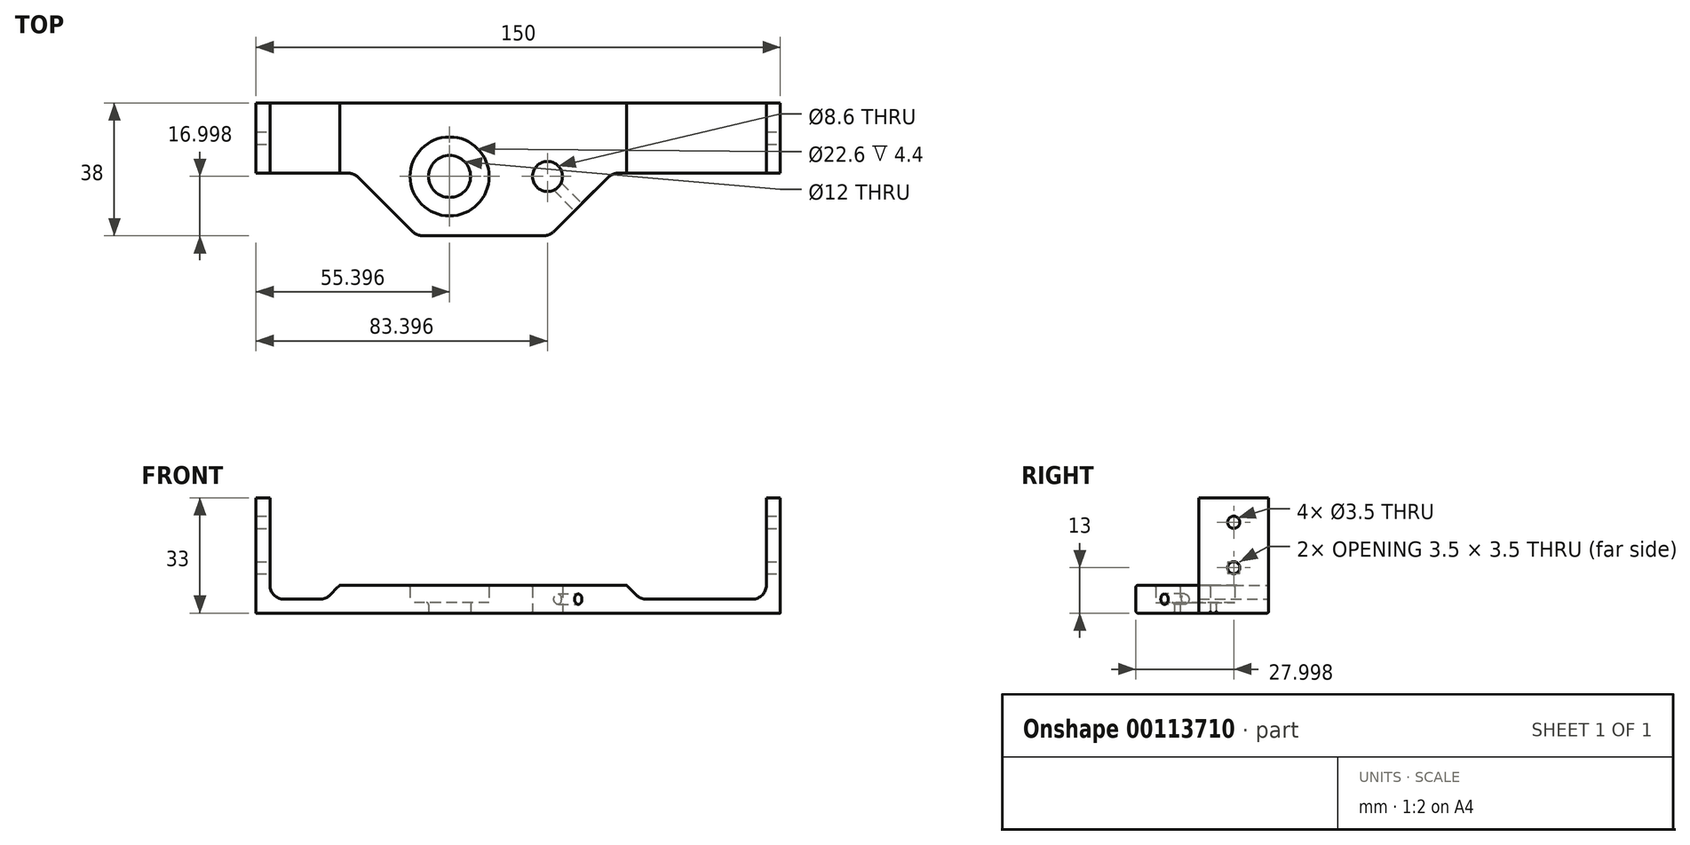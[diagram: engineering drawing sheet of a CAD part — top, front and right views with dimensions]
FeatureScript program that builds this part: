
annotation { "Feature Type Name" : "Feature", "Feature Type Description" : "" }
export const myFeature = defineFeature(function(context is Context, id is Id, definition is map)
    precondition{}
    {
        {
            var Q0;
            Q0=qCreatedBy(makeId("Top.planeOp"),FACE);
            var sketch = newSketch(context, id + "F0", { "sketchPlane" : qUnion([Q0])});
            skLineSegment(sketch, "E0.bottom", {"start": v(-77.83, 12.2) * mm, "end": v(72.17, 12.2) * mm});
            skLineSegment(sketch, "E0.left", {"start": v(-77.83, 12.2) * mm, "end": v(-77.83, -7.8) * mm});
            skLineSegment(sketch, "E0.right", {"start": v(72.17, 12.2) * mm, "end": v(72.17, -7.8) * mm});
            skCircle(sketch, "E1", {"center": v(-22.43, -8.8) * mm, "radius": 6 * mm});
            skCircle(sketch, "E2", {"center": v(5.57, -8.8) * mm, "radius": 4.3 * mm});
            skCircle(sketch, "E3", {"center": v(-22.43, -8.8) * mm, "radius": 11.3 * mm});
            skLineSegment(sketch, "E4", {"start": v(-77.83, -7.8) * mm, "end": v(-49.83, -7.8) * mm});
            skLineSegment(sketch, "E5", {"start": v(-49.83, -7.8) * mm, "end": v(-31.83, -25.8) * mm});
            skLineSegment(sketch, "E6", {"start": v(-31.83, -25.8) * mm, "end": v(6.17, -25.8) * mm});
            skLineSegment(sketch, "E7", {"start": v(6.17, -25.8) * mm, "end": v(24.17, -7.8) * mm});
            skLineSegment(sketch, "E8", {"start": v(24.17, -7.8) * mm, "end": v(72.17, -7.8) * mm});
            skSolve(sketch);
        }
        {
            var Q0;
            Q0=makeQuery(id+"F0.imprint","IMPRINT",FACE,{"disambiguationData":[TD([[makeQuery(id+"F0.imprint","IMPRINT",EDGE,{"derivedFrom":sQuery(id+"F0.wireOp",EDGE,"E0.bottom")}),-1.0]])]});
            extrude(context, id + "F1", {"entities" : qUnion([Q0]), "depth" : 8 * mm});
        }
        {
            var Q0;
            Q0=makeQuery(id+"F0.imprint","IMPRINT",FACE,{"disambiguationData":[TD([[makeQuery(id+"F0.imprint","IMPRINT",EDGE,{"derivedFrom":sQuery(id+"F0.wireOp",EDGE,"E1")}),-1.0]])]});
            extrude(context, id + "F2", {"entities" : qUnion([Q0]), "operationType" : NewBodyOperationType.ADD, "depth" : 3 * mm});
        }
        {
            var Q0;
            Q0=makeQuery(id+"F1.opExtrude","CAP_FACE",FACE,{"disambiguationData":[OSD([sQuery(id+"F0.wireOp",EDGE,"E0.bottom"),sQuery(id+"F0.wireOp",EDGE,"E0.left"),sQuery(id+"F0.wireOp",EDGE,"E0.right"),sQuery(id+"F0.wireOp",EDGE,"E2"),sQuery(id+"F0.wireOp",EDGE,"E3"),sQuery(id+"F0.wireOp",EDGE,"E4"),sQuery(id+"F0.wireOp",EDGE,"E5"),sQuery(id+"F0.wireOp",EDGE,"E6"),sQuery(id+"F0.wireOp",EDGE,"E7"),sQuery(id+"F0.wireOp",EDGE,"E8")])],"isStart":false});
            var sketch = newSketch(context, id + "F3", { "sketchPlane" : qUnion([Q0])});
            skCircle(sketch, "E9", {"center": v(-22.43, -8.8) * mm, "radius": 13 * mm});
            skCircle(sketch, "E10", {"center": v(5.57, -8.8) * mm, "radius": 5.5 * mm});
            skSolve(sketch);
        }
        {
            var Q0;
            Q0=makeQuery(id+"F3.imprint","IMPRINT",FACE,{"disambiguationData":[TD([[makeQuery(id+"F3.imprint","IMPRINT",EDGE,{"derivedFrom":sQuery(id+"F3.wireOp",EDGE,"E9")}),-1.0]])]});
            var sketch = newSketch(context, id + "F4", { "sketchPlane" : qUnion([Q0])});
            skLineSegment(sketch, "E11.bottom", {"start": v(72.17, -7.8) * mm, "end": v(68.17, -7.8) * mm});
            skLineSegment(sketch, "E11.top", {"start": v(72.17, 12.2) * mm, "end": v(68.17, 12.2) * mm});
            skLineSegment(sketch, "E11.left", {"start": v(72.17, -7.8) * mm, "end": v(72.17, 12.2) * mm});
            skLineSegment(sketch, "E11.right", {"start": v(68.17, -7.8) * mm, "end": v(68.17, 12.2) * mm});
            skLineSegment(sketch, "E12.bottom", {"start": v(-73.83, -7.8) * mm, "end": v(-77.83, -7.8) * mm});
            skLineSegment(sketch, "E12.top", {"start": v(-73.83, 12.2) * mm, "end": v(-77.83, 12.2) * mm});
            skLineSegment(sketch, "E12.left", {"start": v(-73.83, -7.8) * mm, "end": v(-73.83, 12.2) * mm});
            skLineSegment(sketch, "E12.right", {"start": v(-77.83, -7.8) * mm, "end": v(-77.83, 12.2) * mm});
            skSolve(sketch);
        }
        {
            var Q0;
            Q0=makeQuery(id+"F4.imprint","IMPRINT",FACE,{"disambiguationData":[TD([[makeQuery(id+"F4.imprint","IMPRINT",EDGE,{"derivedFrom":sQuery(id+"F4.wireOp",EDGE,"E11.bottom")}),1.0]])]});
            var Q1;
            Q1=makeQuery(id+"F4.imprint","IMPRINT",FACE,{"disambiguationData":[TD([[makeQuery(id+"F4.imprint","IMPRINT",EDGE,{"derivedFrom":sQuery(id+"F4.wireOp",EDGE,"E12.bottom")}),1.0]])]});
            extrude(context, id + "F5", {"entities" : qUnion([Q0, Q1]), "operationType" : NewBodyOperationType.ADD, "depth" : 25 * mm});
        }
        {
            var Q0;
            Q0=makeQuery(id+"F5.boolean.opBoolean","MERGE",FACE,{"derivedFrom":[makeQuery(id+"F1.opExtrude","SWEPT_FACE",FACE,{"disambiguationData":[OSD([sQuery(id+"F0.wireOp",EDGE,"E0.bottom")])]}),makeQuery(id+"F5.opExtrude","SWEPT_FACE",FACE,{"disambiguationData":[OSD([sQuery(id+"F4.wireOp",EDGE,"E11.top")])]}),makeQuery(id+"F5.opExtrude","SWEPT_FACE",FACE,{"disambiguationData":[OSD([sQuery(id+"F4.wireOp",EDGE,"E12.top")])]})]});
            var sketch = newSketch(context, id + "F6", { "sketchPlane" : qUnion([Q0])});
            skLineSegment(sketch, "E13", {"start": v(-68.17, 8) * mm, "end": v(-68.17, 4) * mm});
            skLineSegment(sketch, "E14", {"start": v(-68.17, 4) * mm, "end": v(-32.17, 4) * mm});
            skLineSegment(sketch, "E15", {"start": v(-32.17, 4) * mm, "end": v(-28.17, 8) * mm});
            skLineSegment(sketch, "E16", {"start": v(73.83, 8) * mm, "end": v(73.83, 4) * mm});
            skLineSegment(sketch, "E17", {"start": v(73.83, 4) * mm, "end": v(57.83, 4) * mm});
            skLineSegment(sketch, "E18", {"start": v(57.83, 4) * mm, "end": v(53.83, 8) * mm});
            skLineSegment(sketch, "E19", {"start": v(53.83, 8) * mm, "end": v(73.83, 8) * mm});
            skSolve(sketch);
        }
        {
            var Q0;
            {var subQ0=sQuery(id+"F6.wireOp",EDGE,"E13");Q0=makeQuery(id+"F6.imprint","IMPRINT",FACE,{"disambiguationData":[TD([[makeQuery(id+"F6.imprint","IMPRINT",EDGE,{"derivedFrom":subQ0}),1.0]])]});}
            var Q1;
            Q1=makeQuery(id+"F6.imprint","IMPRINT",FACE,{"disambiguationData":[TD([[makeQuery(id+"F6.imprint","IMPRINT",EDGE,{"derivedFrom":sQuery(id+"F6.wireOp",EDGE,"E16")}),-1.0]])]});
            extrude(context, id + "F7", {"entities" : qUnion([Q0, Q1]), "operationType" : NewBodyOperationType.REMOVE, "oppositeDirection" : true, "depth" : 25 * mm});
        }
        {
            var Q0;
            Q0=makeQuery(id+"F2.opExtrude","CAP_EDGE",EDGE,{"disambiguationData":[OSD([sQuery(id+"F0.wireOp",EDGE,"E1")])],"isStart":true});
            var Q1;
            Q1=makeQuery(id+"F1.opExtrude","CAP_EDGE",EDGE,{"disambiguationData":[OSD([sQuery(id+"F0.wireOp",EDGE,"E2")])],"isStart":true});
            var Q2;
            Q2=makeQuery(id+"F1.opExtrude","CAP_EDGE",EDGE,{"disambiguationData":[OSD([sQuery(id+"F0.wireOp",EDGE,"E3")])],"isStart":false});
            var Q3;
            Q3=makeQuery(id+"F2.opExtrude","CAP_EDGE",EDGE,{"disambiguationData":[OSD([sQuery(id+"F0.wireOp",EDGE,"E1")])],"isStart":false});
            var Q4;
            Q4=makeQuery(id+"F1.opExtrude","CAP_EDGE",EDGE,{"disambiguationData":[OSD([sQuery(id+"F0.wireOp",EDGE,"E2")])],"isStart":false});
            fillet(context, id + "F8", {"entities" : qUnion([Q0, Q1, Q2, Q3, Q4]), "radius" : 0.6 * mm, "tangentPropagation" : true, "allowEdgeOverflow" : false});
        }
        {
            var Q0;
            Q0=makeQuery(id+"F1.opExtrude","SWEPT_EDGE",EDGE,{"disambiguationData":[OSD([sQuery(id+"F0.wireOp",EDGE,"E4"),sQuery(id+"F0.wireOp",EDGE,"E5")])]});
            var Q1;
            Q1=makeQuery(id+"F1.opExtrude","SWEPT_EDGE",EDGE,{"disambiguationData":[OSD([sQuery(id+"F0.wireOp",EDGE,"E5"),sQuery(id+"F0.wireOp",EDGE,"E6")])]});
            var Q2;
            Q2=makeQuery(id+"F1.opExtrude","SWEPT_EDGE",EDGE,{"disambiguationData":[OSD([sQuery(id+"F0.wireOp",EDGE,"E6"),sQuery(id+"F0.wireOp",EDGE,"E7")])]});
            var Q3;
            Q3=makeQuery(id+"F1.opExtrude","SWEPT_EDGE",EDGE,{"disambiguationData":[OSD([sQuery(id+"F0.wireOp",EDGE,"E7"),sQuery(id+"F0.wireOp",EDGE,"E8")])]});
            fillet(context, id + "F9", {"entities" : qUnion([Q0, Q1, Q2, Q3]), "radius" : 5 * mm, "tangentPropagation" : true, "allowEdgeOverflow" : false});
        }
        {
            var Q0;
            Q0=makeQuery(id+"F7.boolean.opBoolean","COPY",EDGE,{"derivedFrom":makeQuery(id+"F7.opExtrude","SWEPT_EDGE",EDGE,{"disambiguationData":[OSD([sQuery(id+"F6.wireOp",EDGE,"E13"),sQuery(id+"F6.wireOp",EDGE,"E14")])]})});
            var Q1;
            Q1=makeQuery(id+"F7.boolean.opBoolean","COPY",EDGE,{"derivedFrom":makeQuery(id+"F7.opExtrude","SWEPT_EDGE",EDGE,{"disambiguationData":[OSD([sQuery(id+"F6.wireOp",EDGE,"E16"),sQuery(id+"F6.wireOp",EDGE,"E17")])]})});
            var Q2;
            Q2=makeQuery(id+"F7.boolean.opBoolean","COPY",EDGE,{"derivedFrom":makeQuery(id+"F7.opExtrude","SWEPT_EDGE",EDGE,{"disambiguationData":[OSD([sQuery(id+"F6.wireOp",EDGE,"E14"),sQuery(id+"F6.wireOp",EDGE,"E15")])]})});
            var Q3;
            Q3=makeQuery(id+"F7.boolean.opBoolean","COPY",EDGE,{"derivedFrom":makeQuery(id+"F7.opExtrude","SWEPT_EDGE",EDGE,{"disambiguationData":[OSD([sQuery(id+"F0.wireOp",EDGE,"E0.bottom"),sQuery(id+"F6.wireOp",EDGE,"E15")])]})});
            var Q4;
            Q4=makeQuery(id+"F7.boolean.opBoolean","COPY",EDGE,{"derivedFrom":makeQuery(id+"F7.opExtrude","SWEPT_EDGE",EDGE,{"disambiguationData":[OSD([sQuery(id+"F0.wireOp",EDGE,"E0.bottom"),sQuery(id+"F6.wireOp",EDGE,"E18"),sQuery(id+"F6.wireOp",EDGE,"E19")])]})});
            var Q5;
            Q5=makeQuery(id+"F7.boolean.opBoolean","COPY",EDGE,{"derivedFrom":makeQuery(id+"F7.opExtrude","SWEPT_EDGE",EDGE,{"disambiguationData":[OSD([sQuery(id+"F6.wireOp",EDGE,"E17"),sQuery(id+"F6.wireOp",EDGE,"E18")])]})});
            fillet(context, id + "F10", {"entities" : qUnion([Q0, Q1, Q2, Q3, Q4, Q5]), "radius" : 4 * mm, "tangentPropagation" : true, "allowEdgeOverflow" : false});
        }
        {
            var Q0;
            Q0=makeQuery(id+"F5.boolean.opBoolean","MERGE",FACE,{"derivedFrom":[makeQuery(id+"F1.opExtrude","SWEPT_FACE",FACE,{"disambiguationData":[OSD([sQuery(id+"F0.wireOp",EDGE,"E0.right")])]}),makeQuery(id+"F5.opExtrude","SWEPT_FACE",FACE,{"disambiguationData":[OSD([sQuery(id+"F4.wireOp",EDGE,"E11.left")])]})]});
            var sketch = newSketch(context, id + "F11", { "sketchPlane" : qUnion([Q0])});
            skCircle(sketch, "E20", {"center": v(2.2, 26) * mm, "radius": 1.75 * mm});
            skCircle(sketch, "E21.0.1.0", {"center": v(2.2, 13) * mm, "radius": 1.75 * mm});
            skLineSegment(sketch, "E21.direction1", {"start": v(2.2, 26) * mm, "end": v(27.2, 26) * mm, "construction": true});
            skLineSegment(sketch, "E21.direction2", {"start": v(2.2, 26) * mm, "end": v(2.2, 13) * mm, "construction": true});
            skLineSegment(sketch, "E22", {"start": v(2.2, 33) * mm, "end": v(2.2, 0) * mm, "construction": true});
            skSolve(sketch);
        }
        {
            var Q0;
            Q0=makeQuery(id+"F11.imprint","IMPRINT",FACE,{"disambiguationData":[TD([[makeQuery(id+"F11.imprint","IMPRINT",EDGE,{"derivedFrom":sQuery(id+"F11.wireOp",EDGE,"E20")}),1.0]])]});
            var Q1;
            Q1=makeQuery(id+"F11.imprint","IMPRINT",FACE,{"disambiguationData":[TD([[makeQuery(id+"F11.imprint","IMPRINT",EDGE,{"derivedFrom":sQuery(id+"F11.wireOp",EDGE,"E21.0.1.0")}),1.0]])]});
            extrude(context, id + "F12", {"entities" : qUnion([Q0, Q1]), "operationType" : NewBodyOperationType.REMOVE, "endBound" : BoundingType.THROUGH_ALL, "oppositeDirection" : true, "depth" : 25 * mm});
        }
        {
            var Q0;
            {var subQ0=sQuery(id+"F0.wireOp",EDGE,"E2");var subQ1=sQuery(id+"F0.wireOp",EDGE,"E5");var subQ2=sQuery(id+"F0.wireOp",EDGE,"E4");Q0=makeQuery(id+"F9.opFillet","BLEND_EDGE",EDGE,{"blendedFrom":[makeQuery(id+"F1.opExtrude","SWEPT_EDGE",EDGE,{"disambiguationData":[OSD([subQ2,subQ1])]}),makeQuery(id+"F9esH5csFbs3Src_1.boolean.opBoolean","MERGE",FACE,{"derivedFrom":[makeQuery(id+"F1.opExtrude","CAP_FACE",FACE,{"disambiguationData":[OSD([sQuery(id+"F0.wireOp",EDGE,"E0.bottom"),sQuery(id+"F0.wireOp",EDGE,"E0.left"),sQuery(id+"F0.wireOp",EDGE,"E0.right"),subQ0,sQuery(id+"F0.wireOp",EDGE,"E3"),subQ2,subQ1,sQuery(id+"F0.wireOp",EDGE,"E6"),sQuery(id+"F0.wireOp",EDGE,"E7"),sQuery(id+"F0.wireOp",EDGE,"E8")])],"isStart":false}),makeQuery(id+"F9esH5csFbs3Src_1.opExtrude","CAP_FACE",FACE,{"disambiguationData":[OSD([subQ0])],"isStart":true})]})],"blendedInto":[makeQuery(id+"F9esH5csFbs3Src_1.boolean.opBoolean","MERGE",FACE,{"derivedFrom":[makeQuery(id+"F1.opExtrude","CAP_FACE",FACE,{"disambiguationData":[OSD([sQuery(id+"F0.wireOp",EDGE,"E0.bottom"),sQuery(id+"F0.wireOp",EDGE,"E0.left"),sQuery(id+"F0.wireOp",EDGE,"E0.right"),subQ0,sQuery(id+"F0.wireOp",EDGE,"E3"),subQ2,subQ1,sQuery(id+"F0.wireOp",EDGE,"E6"),sQuery(id+"F0.wireOp",EDGE,"E7"),sQuery(id+"F0.wireOp",EDGE,"E8")])],"isStart":false}),makeQuery(id+"F9esH5csFbs3Src_1.opExtrude","CAP_FACE",FACE,{"disambiguationData":[OSD([subQ0])],"isStart":true})]})]});}
            var Q1;
            {var subQ0=sQuery(id+"F0.wireOp",EDGE,"E3");var subQ1=sQuery(id+"F0.wireOp",EDGE,"E5");var subQ2=sQuery(id+"F0.wireOp",EDGE,"E4");Q1=makeQuery(id+"F9.opFillet","BLEND_EDGE",EDGE,{"blendedFrom":[makeQuery(id+"F1.opExtrude","SWEPT_EDGE",EDGE,{"disambiguationData":[OSD([subQ2,subQ1])]}),makeQuery(id+"F2.boolean.opBoolean","MERGE",FACE,{"derivedFrom":[makeQuery(id+"F1.opExtrude","CAP_FACE",FACE,{"disambiguationData":[OSD([sQuery(id+"F0.wireOp",EDGE,"E0.bottom"),sQuery(id+"F0.wireOp",EDGE,"E0.left"),sQuery(id+"F0.wireOp",EDGE,"E0.right"),sQuery(id+"F0.wireOp",EDGE,"E2"),subQ0,subQ2,subQ1,sQuery(id+"F0.wireOp",EDGE,"E6"),sQuery(id+"F0.wireOp",EDGE,"E7"),sQuery(id+"F0.wireOp",EDGE,"E8")])],"isStart":true}),makeQuery(id+"F2.opExtrude","CAP_FACE",FACE,{"disambiguationData":[OSD([sQuery(id+"F0.wireOp",EDGE,"E1"),subQ0])],"isStart":true})]})],"blendedInto":[makeQuery(id+"F2.boolean.opBoolean","MERGE",FACE,{"derivedFrom":[makeQuery(id+"F1.opExtrude","CAP_FACE",FACE,{"disambiguationData":[OSD([sQuery(id+"F0.wireOp",EDGE,"E0.bottom"),sQuery(id+"F0.wireOp",EDGE,"E0.left"),sQuery(id+"F0.wireOp",EDGE,"E0.right"),sQuery(id+"F0.wireOp",EDGE,"E2"),subQ0,subQ2,subQ1,sQuery(id+"F0.wireOp",EDGE,"E6"),sQuery(id+"F0.wireOp",EDGE,"E7"),sQuery(id+"F0.wireOp",EDGE,"E8")])],"isStart":true}),makeQuery(id+"F2.opExtrude","CAP_FACE",FACE,{"disambiguationData":[OSD([sQuery(id+"F0.wireOp",EDGE,"E1"),subQ0])],"isStart":true})]})]});}
            var Q2;
            Q2=makeQuery(id+"F1.opExtrude","CAP_EDGE",EDGE,{"disambiguationData":[OSD([sQuery(id+"F0.wireOp",EDGE,"E0.bottom")])],"isStart":false});
            var Q3;
            Q3=makeQuery(id+"F1.opExtrude","CAP_EDGE",EDGE,{"disambiguationData":[OSD([sQuery(id+"F0.wireOp",EDGE,"E0.bottom")])],"isStart":true});
            fillet(context, id + "F13", {"entities" : qUnion([Q0, Q1, Q2, Q3]), "radius" : 0.6 * mm, "tangentPropagation" : true, "allowEdgeOverflow" : false});
        }
        {
            var Q0;
            Q0=makeQuery(id+"F1.opExtrude","SWEPT_FACE",FACE,{"disambiguationData":[OSD([sQuery(id+"F0.wireOp",EDGE,"E7")])]});
            var sketch = newSketch(context, id + "F14", { "sketchPlane" : qUnion([Q0])});
            skLineSegment(sketch, "E23", {"start": v(-2.3, 0.6) * mm, "end": v(-2.3, 7.4) * mm, "construction": true});
            skCircle(sketch, "E24", {"center": v(-2.3, 4) * mm, "radius": 1.5 * mm});
            skSolve(sketch);
        }
        {
            var Q0;
            Q0=makeQuery(id+"F14.imprint","IMPRINT",FACE,{"disambiguationData":[TD([[makeQuery(id+"F14.imprint","IMPRINT",EDGE,{"derivedFrom":sQuery(id+"F14.wireOp",EDGE,"E24")}),1.0]])]});
            extrude(context, id + "F15", {"entities" : qUnion([Q0]), "operationType" : NewBodyOperationType.REMOVE, "oppositeDirection" : true, "depth" : 15 * mm});
        }
    });
